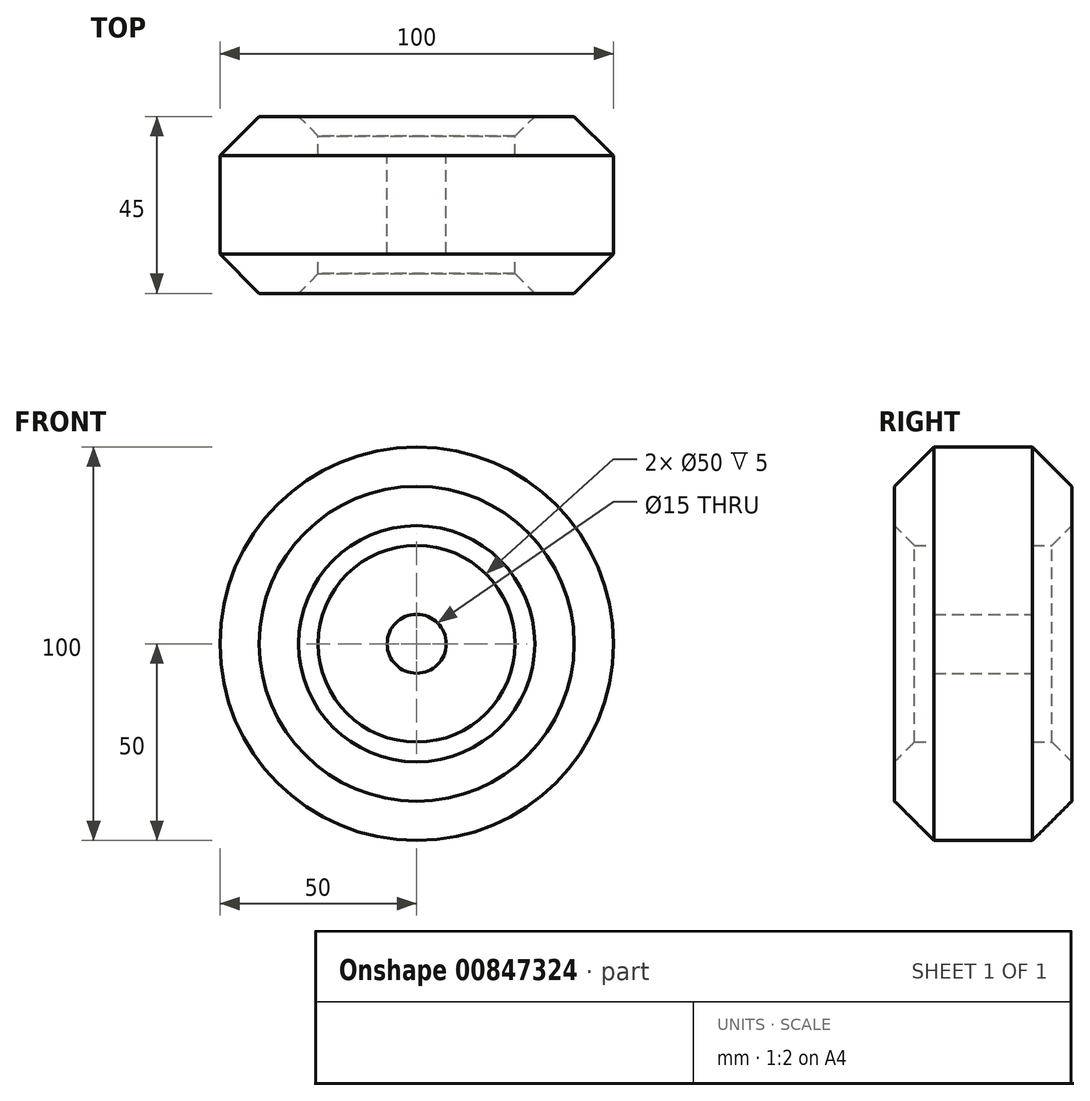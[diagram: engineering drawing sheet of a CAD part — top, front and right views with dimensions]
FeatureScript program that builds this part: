
annotation { "Feature Type Name" : "Feature", "Feature Type Description" : "" }
export const myFeature = defineFeature(function(context is Context, id is Id, definition is map)
    precondition{}
    {
        {
            var Q0;
            Q0=qCreatedBy(makeId("Front.planeOp"),FACE);
            var sketch = newSketch(context, id + "F0", { "sketchPlane" : qUnion([Q0])});
            skCircle(sketch, "E0", {"center": v(0, 0) * mm, "radius": 25 * mm});
            skCircle(sketch, "E1", {"center": v(0, 0) * mm, "radius": 50 * mm});
            skCircle(sketch, "E2", {"center": v(0, 0) * mm, "radius": 7.5 * mm});
            skSolve(sketch);
        }
        {
            var Q0;
            Q0=makeQuery(id+"F0.imprint","IMPRINT",FACE,{"disambiguationData":[TD([[makeQuery(id+"F0.imprint","IMPRINT",EDGE,{"derivedFrom":sQuery(id+"F0.wireOp",EDGE,"E0")}),-1.0]])]});
            extrude(context, id + "F1", {"entities" : qUnion([Q0]), "endBound" : BoundingType.SYMMETRIC, "depth" : 45 * mm, "offsetDistance" : 25 * mm});
        }
        {
            var Q0;
            Q0=makeQuery(id+"F0.imprint","IMPRINT",FACE,{"disambiguationData":[TD([[makeQuery(id+"F0.imprint","IMPRINT",EDGE,{"derivedFrom":sQuery(id+"F0.wireOp",EDGE,"E0")}),1.0]])]});
            extrude(context, id + "F2", {"entities" : qUnion([Q0]), "operationType" : NewBodyOperationType.ADD, "endBound" : BoundingType.SYMMETRIC, "depth" : 25 * mm, "offsetDistance" : 25 * mm});
        }
        {
            var Q0;
            Q0=makeQuery(id+"F1.opExtrude","CAP_EDGE",EDGE,{"disambiguationData":[OSD([sQuery(id+"F0.wireOp",EDGE,"E1")])],"isStart":false});
            var Q1;
            Q1=makeQuery(id+"F1.opExtrude","CAP_EDGE",EDGE,{"disambiguationData":[OSD([sQuery(id+"F0.wireOp",EDGE,"E1")])],"isStart":true});
            chamfer(context, id + "F3", {"entities" : qUnion([Q0, Q1]), "width" : 10 * mm, "tangentPropagation" : true});
        }
        {
            var Q0;
            Q0=makeQuery(id+"F1.opExtrude","CAP_EDGE",EDGE,{"disambiguationData":[OSD([sQuery(id+"F0.wireOp",EDGE,"E0")])],"isStart":false});
            var Q1;
            Q1=makeQuery(id+"F1.opExtrude","CAP_EDGE",EDGE,{"disambiguationData":[OSD([sQuery(id+"F0.wireOp",EDGE,"E0")])],"isStart":true});
            chamfer(context, id + "F4", {"entities" : qUnion([Q0, Q1]), "width" : 5 * mm, "tangentPropagation" : true});
        }
    });
